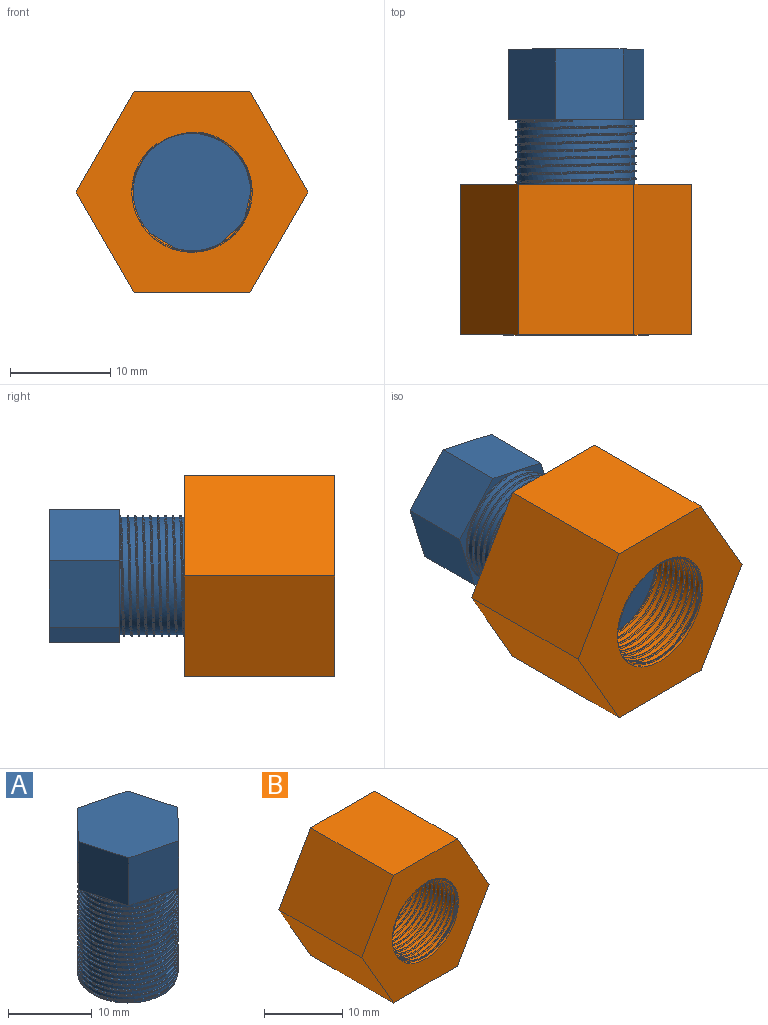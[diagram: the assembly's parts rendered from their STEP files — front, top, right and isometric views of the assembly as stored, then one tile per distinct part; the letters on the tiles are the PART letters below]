
ASSEMBLY  parts=2 mates=1
PART A: 14 faces, bbox 13.4x13.9x22.1 mm
  f0: bspline ~15.05x13.86mm, area 110.9mm2, adj f2,f3,f4,f13
  f1: bspline ~14.93x13.86mm, area 111.2mm2, adj f2,f3,f4,f13
  f2: cylinder r=6mm len=14.95mm, axis (0,0,-1), area -77.7mm2, adj f0,f1,f4,f13
  f3: cylinder r=5.86mm len=15mm, axis (0,0,1), area 331.4mm2, adj f0,f1,f4,f12,f13
  f4: plane 11.77x11.73mm, normal (0,0,-1), area 108.9mm2, adj f0,f1,f2,f3
  f5: plane 7x6.66mm, normal (0.96,0.27,0), area 48.5mm2, adj f6,f10,f11,f12
  f6: plane 7x6.72mm, normal (0.24,0.97,0), area 48.5mm2, adj f5,f7,f11,f12
  f7: plane 7x4.98mm, normal (-0.72,0.7,0), area 48.5mm2, adj f6,f8,f11,f12
  f8: plane 7x6.66mm, normal (-0.96,-0.27,0), area 48.5mm2, adj f7,f9,f11,f12
  f9: plane 7x6.72mm, normal (-0.24,-0.97,0), area 48.5mm2, adj f8,f10,f11,f12
  f10: plane 7x4.98mm, normal (0.72,-0.7,0), area 48.5mm2, adj f5,f9,f11,f12
  f11: plane 13.44x13.33mm, normal (0,0,1), area 124.7mm2, adj f5,f6,f7,f8,f9,f10
  f12: plane 13.44x13.33mm, normal (0,0,-1), area 16.9mm2, adj f3,f5,f6,f7,f8,f9,f10
  f13: plane 0.2x0.14mm, normal (0,1,0), area 0mm2, adj f0,f1,f2,f3
PART B: 13 faces, bbox 23.1x15.1x20 mm
  f0: cylinder r=6mm len=15mm, axis (0,1,0), area 339.3mm2, adj f7,f8,f9,f10,f11
  f1: plane 15x10mm, normal (0.87,0,0.5), area 173.2mm2, adj f2,f6,f7,f8
  f2: plane 15x11.55mm, normal (0,0,1), area 173.2mm2, adj f1,f3,f7,f8
  f3: plane 15x10mm, normal (-0.87,0,0.5), area 173.2mm2, adj f2,f4,f7,f8
  f4: plane 15x10mm, normal (-0.87,0,-0.5), area 173.2mm2, adj f3,f5,f7,f8
  f5: plane 15x11.55mm, normal (0,0,-1), area 173.2mm2, adj f4,f6,f7,f8
  f6: plane 15x10mm, normal (0.87,0,-0.5), area 173.2mm2, adj f1,f5,f7,f8
  f7: plane 23.09x20mm, normal (0,-1,0), area 234.4mm2, adj f0,f1,f2,f3,f4,f5,f6,f10
  f8: plane 23.09x20mm, normal (0,1,0), area 233.3mm2, adj f0,f1,f2,f3,f4,f5,f6
  f9: plane 0.2x0.14mm, normal (0,0,1), area 0mm2, adj f0,f10,f11,f12
  f10: bspline ~14.93x13.86mm, area 110.4mm2, adj f0,f7,f9,f12
  f11: bspline ~15.05x13.86mm, area 111.5mm2, adj f0,f7,f9,f12
  f12: cylinder r=5.86mm len=14.95mm, axis (0,-1,0), area -75.9mm2, adj f7,f9,f10,f11
PLACE A rot(axis=(-0.55,-0.59,-0.59),121.9deg) t=(-13.6,13.6,-19.82)mm
PLACE B t=(-13.94,-0.38,-13.97)mm fixed
MATE cylindrical A.f3 <-> B.f0  axis (0,-1,0) through (-13.94,-1.4,-13.97)mm
